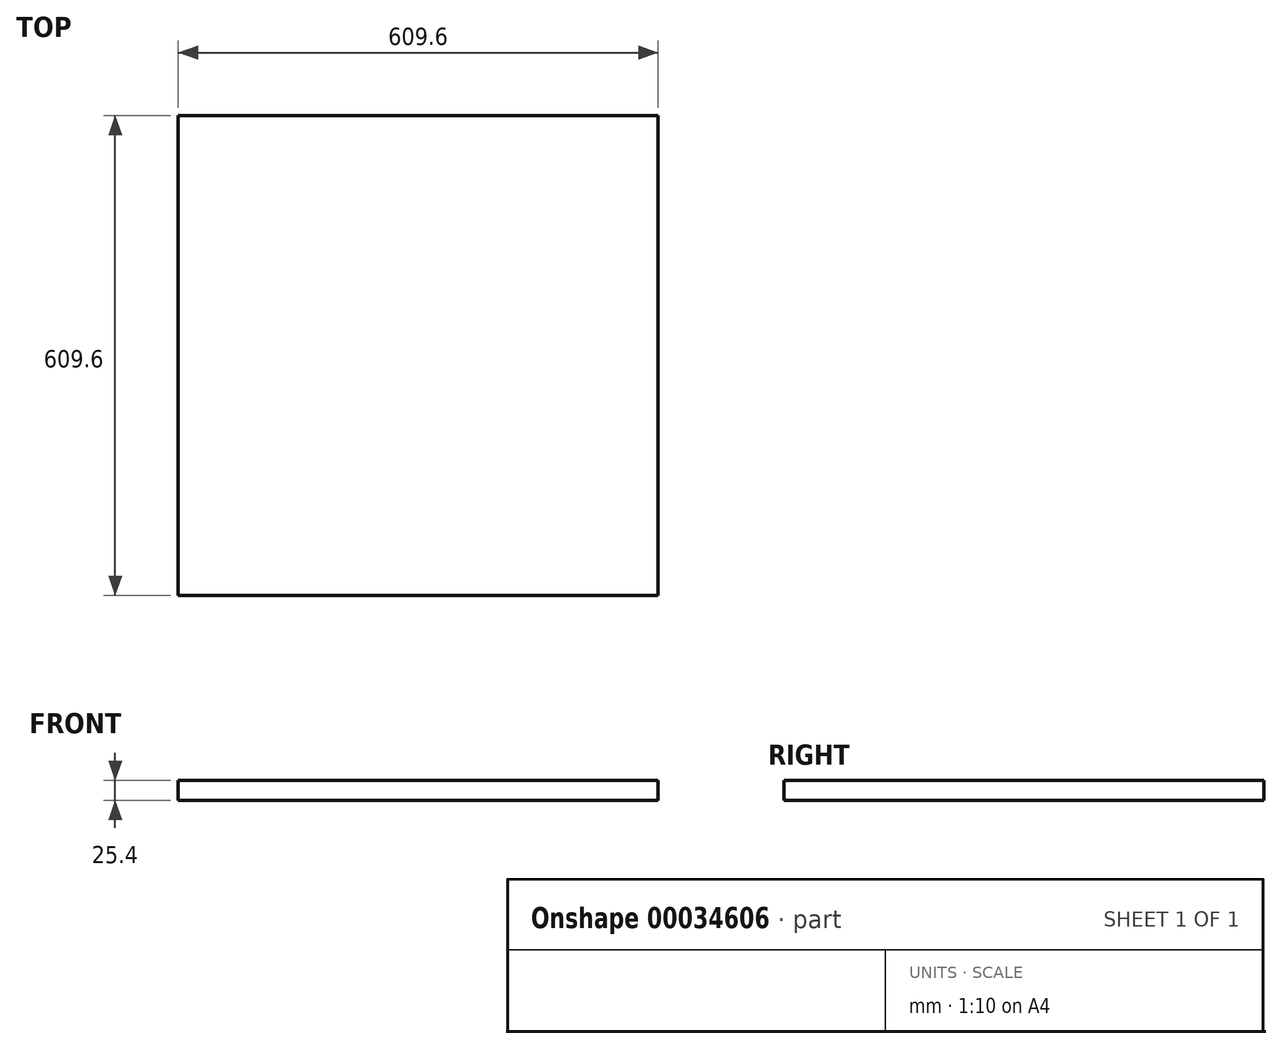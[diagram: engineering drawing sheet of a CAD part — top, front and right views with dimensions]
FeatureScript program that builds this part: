
annotation { "Feature Type Name" : "Feature", "Feature Type Description" : "" }
export const myFeature = defineFeature(function(context is Context, id is Id, definition is map)
    precondition{}
    {
        {
            var Q0;
            Q0=qCreatedBy(makeId("Top.planeOp"),FACE);
            var sketch = newSketch(context, id + "F0", { "sketchPlane" : qUnion([Q0])});
            skLineSegment(sketch, "E0.bottom", {"start": v(0, 0) * mm, "end": v(609.6, 0) * mm});
            skLineSegment(sketch, "E0.top", {"start": v(0, -609.6) * mm, "end": v(609.6, -609.6) * mm});
            skLineSegment(sketch, "E0.left", {"start": v(0, 0) * mm, "end": v(0, -609.6) * mm});
            skLineSegment(sketch, "E0.right", {"start": v(609.6, 0) * mm, "end": v(609.6, -609.6) * mm});
            skSolve(sketch);
        }
        {
            var Q0;
            Q0 = qSketchRegion(id + "F0", true);
            extrude(context, id + "F1", {"entities" : qUnion([Q0]), "depth" : 25.4 * mm});
        }
    });
